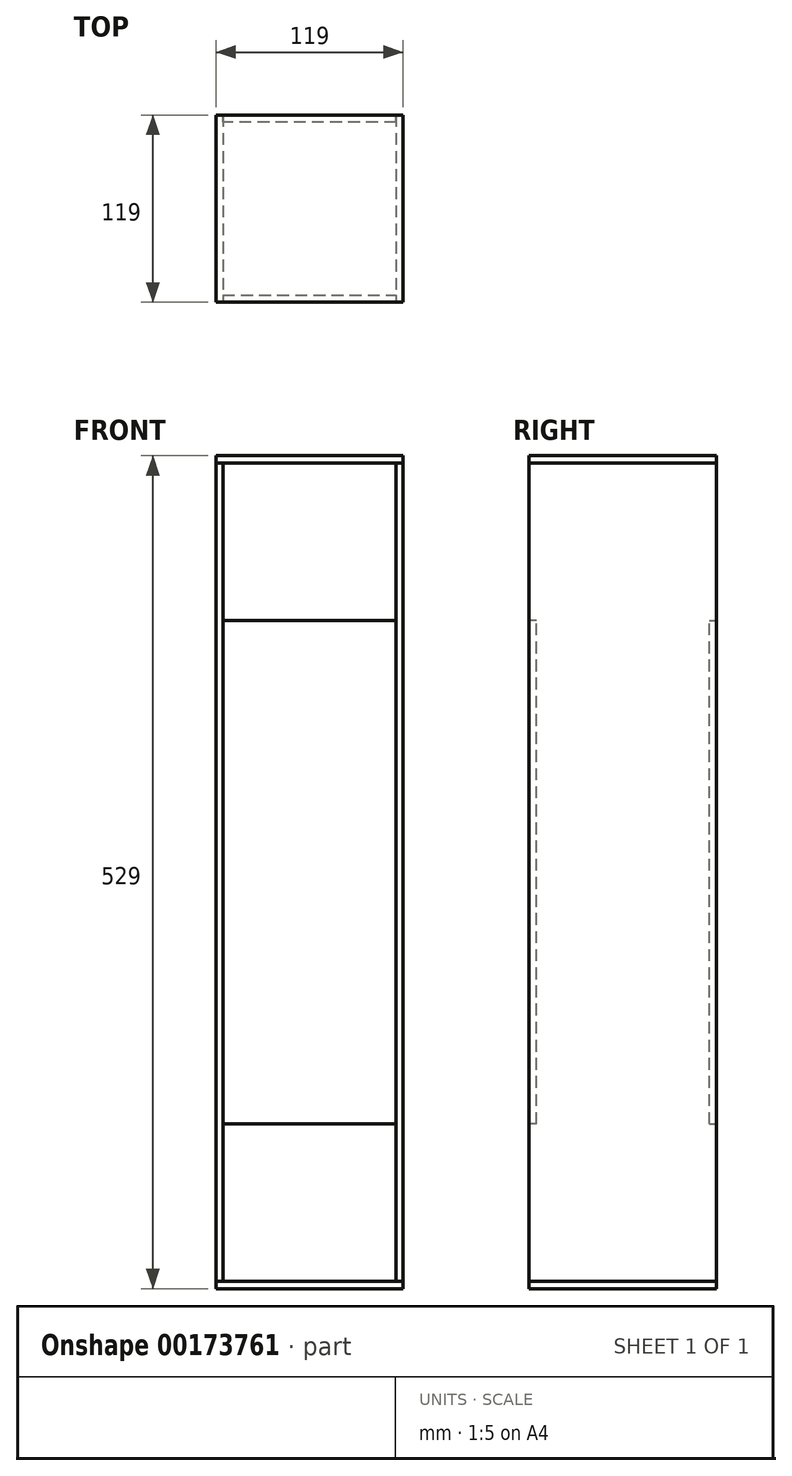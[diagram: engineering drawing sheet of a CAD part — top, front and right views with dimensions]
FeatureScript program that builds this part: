
annotation { "Feature Type Name" : "Feature", "Feature Type Description" : "" }
export const myFeature = defineFeature(function(context is Context, id is Id, definition is map)
    precondition{}
    {
        {
            var Q0;
            Q0=qCreatedBy(makeId("Top.planeOp"),FACE);
            var sketch = newSketch(context, id + "F0", { "sketchPlane" : qUnion([Q0])});
            skLineSegment(sketch, "E0.bottom", {"start": v(-71.73, 57.58) * mm, "end": v(47.27, 57.58) * mm});
            skLineSegment(sketch, "E0.top", {"start": v(-71.73, -61.42) * mm, "end": v(47.27, -61.42) * mm});
            skLineSegment(sketch, "E0.left", {"start": v(-71.73, 57.58) * mm, "end": v(-71.73, -61.42) * mm});
            skLineSegment(sketch, "E0.right", {"start": v(47.27, 57.58) * mm, "end": v(47.27, -61.42) * mm});
            skSolve(sketch);
        }
        {
            var Q0;
            Q0 = qSketchRegion(id + "F0", true);
            extrude(context, id + "F1", {"entities" : qUnion([Q0]), "oppositeDirection" : true, "depth" : 4.5 * mm});
        }
        {
            var Q0;
            Q0=makeQuery(id+"F1.opExtrude","SWEPT_FACE",FACE,{"disambiguationData":[OSD([sQuery(id+"F0.wireOp",EDGE,"E0.right")])]});
            var sketch = newSketch(context, id + "F2", { "sketchPlane" : qUnion([Q0])});
            skLineSegment(sketch, "E1.bottom", {"start": v(-61.42, 0) * mm, "end": v(57.58, 0) * mm});
            skLineSegment(sketch, "E1.top", {"start": v(-61.42, 520) * mm, "end": v(57.58, 520) * mm});
            skLineSegment(sketch, "E1.left", {"start": v(-61.42, 0) * mm, "end": v(-61.42, 520) * mm});
            skLineSegment(sketch, "E1.right", {"start": v(57.58, 0) * mm, "end": v(57.58, 520) * mm});
            skSolve(sketch);
        }
        {
            var Q0;
            Q0 = qSketchRegion(id + "F2", true);
            extrude(context, id + "F3", {"entities" : qUnion([Q0]), "oppositeDirection" : true, "depth" : 4.5 * mm});
        }
        {
            var Q0;
            Q0=makeQuery(id+"F1.opExtrude","SWEPT_FACE",FACE,{"disambiguationData":[OSD([sQuery(id+"F0.wireOp",EDGE,"E0.left")])]});
            var sketch = newSketch(context, id + "F4", { "sketchPlane" : qUnion([Q0])});
            skLineSegment(sketch, "E2.bottom", {"start": v(-57.58, 0) * mm, "end": v(61.42, 0) * mm});
            skLineSegment(sketch, "E2.top", {"start": v(-57.58, 520) * mm, "end": v(61.42, 520) * mm});
            skLineSegment(sketch, "E2.left", {"start": v(-57.58, 0) * mm, "end": v(-57.58, 520) * mm});
            skLineSegment(sketch, "E2.right", {"start": v(61.42, 0) * mm, "end": v(61.42, 520) * mm});
            skSolve(sketch);
        }
        {
            var Q0;
            Q0 = qSketchRegion(id + "F4", true);
            extrude(context, id + "F5", {"entities" : qUnion([Q0]), "oppositeDirection" : true, "depth" : 4.5 * mm});
        }
        {
            var Q0;
            Q0=makeQuery(id+"F3.opExtrude","SWEPT_FACE",FACE,{"disambiguationData":[OSD([sQuery(id+"F2.wireOp",EDGE,"E1.top")])]});
            var sketch = newSketch(context, id + "F6", { "sketchPlane" : qUnion([Q0])});
            skLineSegment(sketch, "E3.bottom", {"start": v(47.27, 57.58) * mm, "end": v(-71.73, 57.58) * mm});
            skLineSegment(sketch, "E3.top", {"start": v(47.27, -61.42) * mm, "end": v(-71.73, -61.42) * mm});
            skLineSegment(sketch, "E3.left", {"start": v(47.27, 57.58) * mm, "end": v(47.27, -61.42) * mm});
            skLineSegment(sketch, "E3.right", {"start": v(-71.73, 57.58) * mm, "end": v(-71.73, -61.42) * mm});
            skSolve(sketch);
        }
        {
            var Q0;
            Q0 = qSketchRegion(id + "F6", true);
            extrude(context, id + "F7", {"entities" : qUnion([Q0]), "depth" : 4.5 * mm});
        }
        {
            var Q0;
            Q0=makeQuery(id+"F5.opExtrude","SWEPT_FACE",FACE,{"disambiguationData":[OSD([sQuery(id+"F4.wireOp",EDGE,"E2.right")])]});
            var sketch = newSketch(context, id + "F8", { "sketchPlane" : qUnion([Q0])});
            skLineSegment(sketch, "E4", {"start": v(-67.23, 0) * mm, "end": v(-67.23, 100) * mm});
            skLineSegment(sketch, "E5.bottom", {"start": v(-67.23, 100) * mm, "end": v(42.77, 100) * mm});
            skLineSegment(sketch, "E5.top", {"start": v(-67.23, 420) * mm, "end": v(42.77, 420) * mm});
            skLineSegment(sketch, "E5.left", {"start": v(-67.23, 100) * mm, "end": v(-67.23, 420) * mm});
            skLineSegment(sketch, "E5.right", {"start": v(42.77, 100) * mm, "end": v(42.77, 420) * mm});
            skSolve(sketch);
        }
        {
            var Q0;
            Q0 = qSketchRegion(id + "F8", true);
            extrude(context, id + "F9", {"entities" : qUnion([Q0]), "oppositeDirection" : true, "depth" : 4.5 * mm});
        }
        {
            var Q0;
            Q0=makeQuery(id+"F3.opExtrude","SWEPT_FACE",FACE,{"disambiguationData":[OSD([sQuery(id+"F2.wireOp",EDGE,"E1.right")])]});
            var sketch = newSketch(context, id + "F10", { "sketchPlane" : qUnion([Q0])});
            skLineSegment(sketch, "E6.bottom", {"start": v(-42.77, 100) * mm, "end": v(67.23, 100) * mm});
            skLineSegment(sketch, "E6.top", {"start": v(-42.77, 420) * mm, "end": v(67.23, 420) * mm});
            skLineSegment(sketch, "E6.left", {"start": v(-42.77, 100) * mm, "end": v(-42.77, 420) * mm});
            skLineSegment(sketch, "E6.right", {"start": v(67.23, 100) * mm, "end": v(67.23, 420) * mm});
            skSolve(sketch);
        }
        {
            var Q0;
            Q0 = qSketchRegion(id + "F10", true);
            extrude(context, id + "F11", {"entities" : qUnion([Q0]), "oppositeDirection" : true, "depth" : 4.5 * mm});
        }
    });
